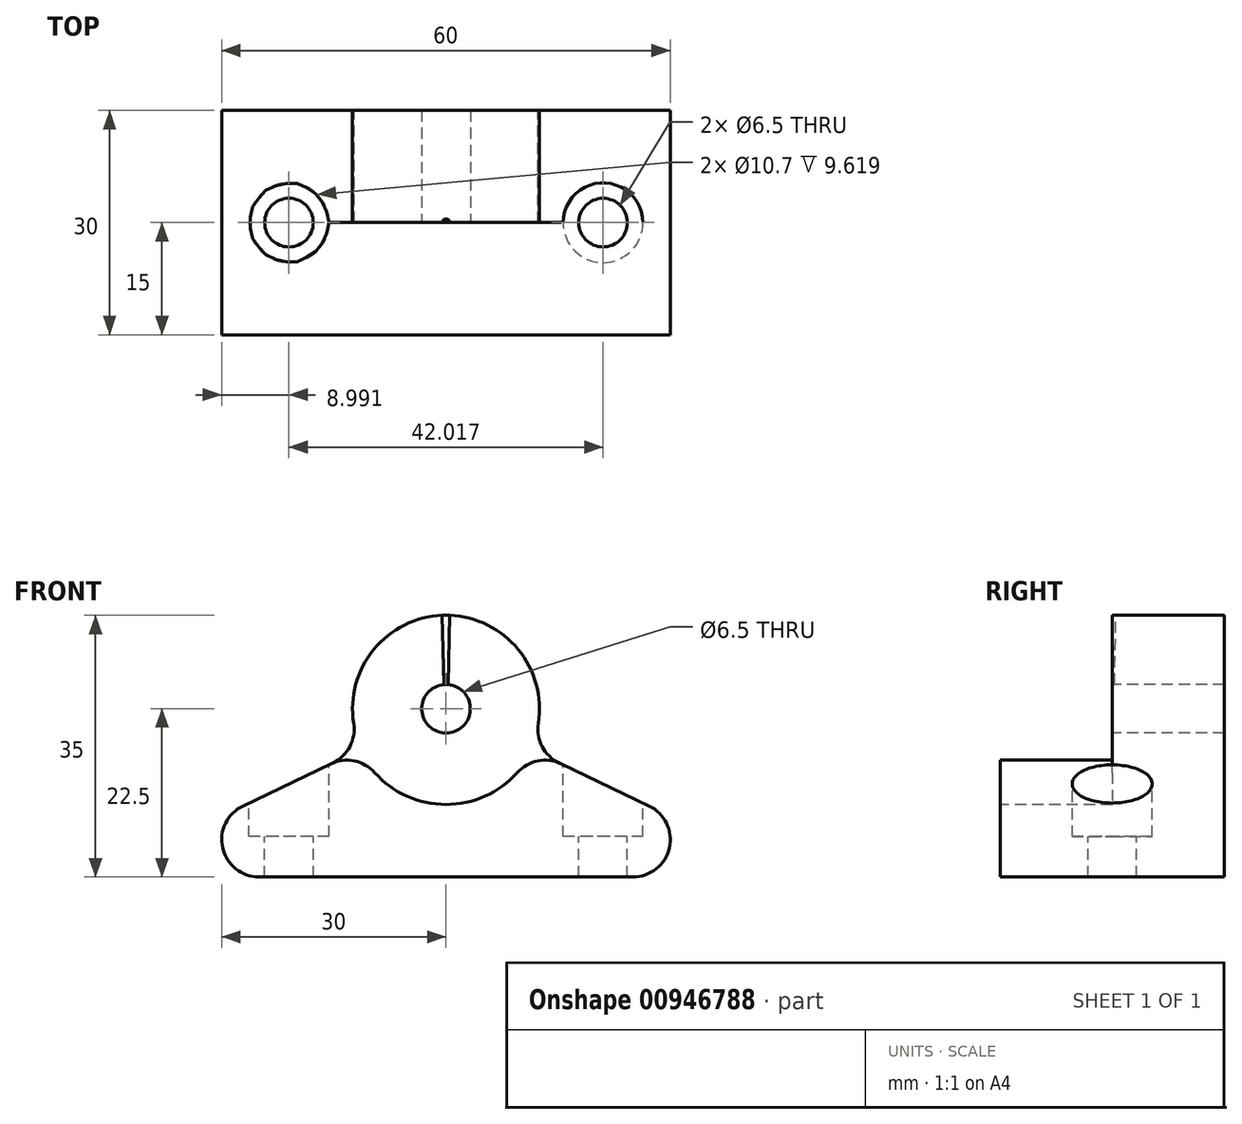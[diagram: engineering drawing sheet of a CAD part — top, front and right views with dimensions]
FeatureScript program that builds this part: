
annotation { "Feature Type Name" : "Feature", "Feature Type Description" : "" }
export const myFeature = defineFeature(function(context is Context, id is Id, definition is map)
    precondition{}
    {
        {
            var Q0;
            Q0=qCreatedBy(makeId("Front.planeOp"),FACE);
            var sketch = newSketch(context, id + "F0", { "sketchPlane" : qUnion([Q0])});
            skLineSegment(sketch, "E0", {"start": v(-25, 0) * mm, "end": v(25, 0) * mm});
            skLineSegment(sketch, "E1", {"start": v(27.16, 9.51) * mm, "end": v(15.13, 15.26) * mm});
            skLineSegment(sketch, "E2", {"start": v(-15.13, 15.26) * mm, "end": v(-27.16, 9.51) * mm});
            skArc(sketch, "E3", {"start": v(12.35, 20.55) * mm, "mid": v(0, 35) * mm, "end": v(-12.35, 20.55) * mm});
            skPoint(sketch, "E4.visualSharp", {"position": v(-47.04, 0) * mm});
            skArc(sketch, "E4.filletArc", {"start": v(-27.16, 9.51) * mm, "mid": v(-29.88, 3.9) * mm, "end": v(-25, 0) * mm});
            skPoint(sketch, "E5.visualSharp", {"position": v(47.04, 0) * mm});
            skArc(sketch, "E5.filletArc", {"start": v(25, 0) * mm, "mid": v(29.88, 3.9) * mm, "end": v(27.16, 9.51) * mm});
            skPoint(sketch, "E6.visualSharp", {"position": v(11.28, 17.1) * mm});
            skArc(sketch, "E6.filletArc", {"start": v(12.35, 20.55) * mm, "mid": v(12.86, 17.45) * mm, "end": v(15.13, 15.26) * mm});
            skPoint(sketch, "E7.visualSharp", {"position": v(-11.28, 17.1) * mm});
            skArc(sketch, "E7.filletArc", {"start": v(-15.13, 15.26) * mm, "mid": v(-12.86, 17.45) * mm, "end": v(-12.35, 20.55) * mm});
            skSolve(sketch);
        }
        {
            var Q0;
            Q0 = qSketchRegion(id + "F0", true);
            extrude(context, id + "F1", {"entities" : qUnion([Q0]), "endBound" : BoundingType.SYMMETRIC, "depth" : 30 * mm, "offsetDistance" : 25 * mm});
        }
        {
            var Q0;
            Q0=makeQuery(id+"F1.opExtrude","CAP_FACE",FACE,{"disambiguationData":[OSD([sQuery(id+"F0.wireOp",EDGE,"E0"),sQuery(id+"F0.wireOp",EDGE,"E1"),sQuery(id+"F0.wireOp",EDGE,"E2"),sQuery(id+"F0.wireOp",EDGE,"E3"),sQuery(id+"F0.wireOp",EDGE,"E4.filletArc"),sQuery(id+"F0.wireOp",EDGE,"E5.filletArc"),sQuery(id+"F0.wireOp",EDGE,"E6.filletArc"),sQuery(id+"F0.wireOp",EDGE,"E7.filletArc")])],"isStart":false});
            var sketch = newSketch(context, id + "F2", { "sketchPlane" : qUnion([Q0])});
            skCircle(sketch, "E8", {"center": v(0, 22.5) * mm, "radius": 12.8 * mm});
            skSolve(sketch);
        }
        {
            var Q0;
            Q0 = qSketchRegion(id + "F2", true);
            extrude(context, id + "F3", {"entities" : qUnion([Q0]), "operationType" : NewBodyOperationType.REMOVE, "oppositeDirection" : true, "depth" : 15 * mm, "offsetDistance" : 25 * mm});
        }
        {
            var Q0;
            Q0=makeQuery(id+"F3.boolean.opBoolean","INTERSECT",EDGE,{"derivedFrom":[makeQuery(id+"F1.opExtrude","SWEPT_FACE",FACE,{"disambiguationData":[OSD([sQuery(id+"F0.wireOp",EDGE,"E7.filletArc")])]}),makeQuery(id+"F3.opExtrude","SWEPT_FACE",FACE,{"disambiguationData":[OSD([sQuery(id+"F2.wireOp",EDGE,"E8")])]})]});
            var Q1;
            Q1=makeQuery(id+"F3.boolean.opBoolean","INTERSECT",EDGE,{"derivedFrom":[makeQuery(id+"F1.opExtrude","SWEPT_FACE",FACE,{"disambiguationData":[OSD([sQuery(id+"F0.wireOp",EDGE,"E6.filletArc")])]}),makeQuery(id+"F3.opExtrude","SWEPT_FACE",FACE,{"disambiguationData":[OSD([sQuery(id+"F2.wireOp",EDGE,"E8")])]})]});
            fillet(context, id + "F4", {"entities" : qUnion([Q0, Q1]), "radius" : 5 * mm, "tangentPropagation" : true, "allowEdgeOverflow" : false});
        }
        {
            var Q0;
            Q0=makeQuery(id+"F3.boolean.opBoolean","COPY",FACE,{"derivedFrom":makeQuery(id+"F3.opExtrude","CAP_FACE",FACE,{"disambiguationData":[OSD([sQuery(id+"F2.wireOp",EDGE,"E8")])],"isStart":false})});
            var sketch = newSketch(context, id + "F5", { "sketchPlane" : qUnion([Q0])});
            skPoint(sketch, "E9", {"position": v(0, 22.5) * mm});
            skSolve(sketch);
        }
        {
            var Q0;
            Q0=sQuery(id+"F5.wireOp",VERTEX,"E9");
            var Q1;
            Q1=makeQuery(id+"F1.opExtrude","SWEPT_BODY",BODY,{"disambiguationData":[OSD([sQuery(id+"F0.wireOp",EDGE,"E0"),sQuery(id+"F0.wireOp",EDGE,"E1"),sQuery(id+"F0.wireOp",EDGE,"E2"),sQuery(id+"F0.wireOp",EDGE,"E3"),sQuery(id+"F0.wireOp",EDGE,"E4.filletArc"),sQuery(id+"F0.wireOp",EDGE,"E5.filletArc"),sQuery(id+"F0.wireOp",EDGE,"E6.filletArc"),sQuery(id+"F0.wireOp",EDGE,"E7.filletArc")])]});
            hole(context, id + "F6", {"style" : HoleStyle.SIMPLE, "endStyle" : HoleEndStyle.THROUGH, "holeDiameter" : 6.5 * mm, "majorDiameter" : 5 * mm, "isTappedThrough" : true, "tappedDepth" : 12 * mm, "tapClearance" : 3, "locations" : qUnion([Q0]), "scope" : qUnion([Q1])});
        }
        {
            var Q0;
            Q0=qCreatedBy(makeId("Top.planeOp"),FACE);
            cPlane(context, id + "F7", {"entities" : qUnion([Q0]), "cplaneType" : CPlaneType.OFFSET, "offset" : 35 * mm, "width" : 150 * mm, "height" : 150 * mm});
        }
        {
            var Q0;
            Q0=qCreatedBy(id+"F7.planeOp",FACE);
            cPlane(context, id + "F8", {"entities" : qUnion([Q0]), "cplaneType" : CPlaneType.OFFSET, "offset" : 9.27 * mm, "oppositeDirection" : true, "width" : 150 * mm, "height" : 150 * mm});
        }
        {
            var Q0;
            Q0=makeQuery(id+"F1.opExtrude","SWEPT_FACE",FACE,{"disambiguationData":[OSD([sQuery(id+"F0.wireOp",EDGE,"E0")])]});
            cPlane(context, id + "F9", {"entities" : qUnion([Q0]), "cplaneType" : CPlaneType.OFFSET, "offset" : 17 * mm, "oppositeDirection" : true, "width" : 150 * mm, "height" : 150 * mm});
        }
        {
            var Q0;
            Q0=qCreatedBy(id+"F9.planeOp",FACE);
            var sketch = newSketch(context, id + "F10", { "sketchPlane" : qUnion([Q0])});
            skPoint(sketch, "E10", {"position": v(-21, 0) * mm});
            skPoint(sketch, "E11.MirrorP", {"position": v(21, 0) * mm});
            skSolve(sketch);
        }
        {
            var Q0;
            Q0=sQuery(id+"F10.wireOp",VERTEX,"E10");
            var Q1;
            Q1=sQuery(id+"F10.wireOp",VERTEX,"E11.MirrorP");
            var Q2;
            Q2=makeQuery(id+"F1.opExtrude","SWEPT_BODY",BODY,{"disambiguationData":[OSD([sQuery(id+"F0.wireOp",EDGE,"E0"),sQuery(id+"F0.wireOp",EDGE,"E1"),sQuery(id+"F0.wireOp",EDGE,"E2"),sQuery(id+"F0.wireOp",EDGE,"E3"),sQuery(id+"F0.wireOp",EDGE,"E4.filletArc"),sQuery(id+"F0.wireOp",EDGE,"E5.filletArc"),sQuery(id+"F0.wireOp",EDGE,"E6.filletArc"),sQuery(id+"F0.wireOp",EDGE,"E7.filletArc")])]});
            hole(context, id + "F11", {"style" : HoleStyle.C_BORE, "endStyle" : HoleEndStyle.THROUGH, "oppositeDirection" : true, "holeDiameter" : 6.5 * mm, "cBoreDiameter" : 10.7 * mm, "cBoreDepth" : 4.5 * mm, "majorDiameter" : 5 * mm, "isTappedThrough" : true, "tappedDepth" : 12 * mm, "tapClearance" : 3, "locations" : qUnion([Q0, Q1]), "scope" : qUnion([Q2])});
        }
        {
            var Q0;
            Q0=qCreatedBy(id+"F7.planeOp",FACE);
            var sketch = newSketch(context, id + "F12", { "sketchPlane" : qUnion([Q0])});
            skArc(sketch, "E12", {"start": v(0.5, 0) * mm, "mid": v(0, 0.5) * mm, "end": v(-0.5, 0) * mm});
            skLineSegment(sketch, "E13", {"start": v(-0.5, 0) * mm, "end": v(0.5, 0) * mm});
            skSolve(sketch);
        }
        {
            var Q0;
            Q0=qCreatedBy(id+"F8.planeOp",FACE);
            var sketch = newSketch(context, id + "F13", { "sketchPlane" : qUnion([Q0])});
            skArc(sketch, "E14", {"start": v(0.3, 0) * mm, "mid": v(0, 0.3) * mm, "end": v(-0.3, 0) * mm});
            skLineSegment(sketch, "E15", {"start": v(-0.3, 0) * mm, "end": v(0.3, 0) * mm});
            skSolve(sketch);
        }
        {
            var Q1;
            Q1 = qSketchRegion(id + "F12", true);
            var Q2;
            Q2 = qSketchRegion(id + "F13", true);
            loft(context, id + "F14", {"operationType" : NewBodyOperationType.REMOVE, "sheetProfilesArray" : [{ "sheetProfileEntities" : qUnion([Q1]) }, { "sheetProfileEntities" : qUnion([Q2]) }]});
        }
    });
